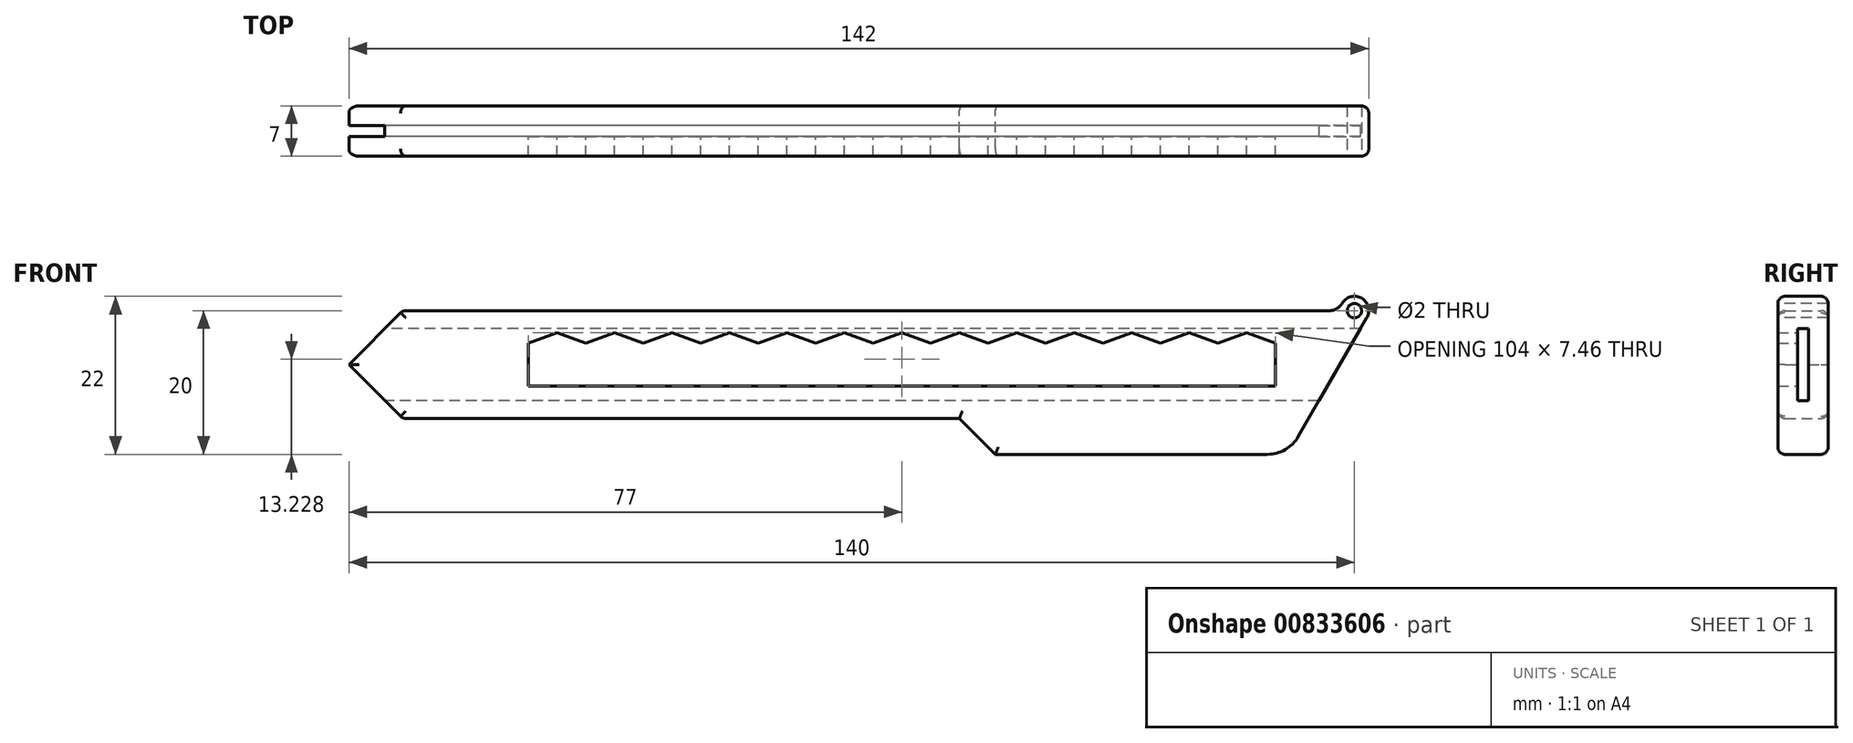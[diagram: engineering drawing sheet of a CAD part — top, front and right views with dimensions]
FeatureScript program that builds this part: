
annotation { "Feature Type Name" : "Feature", "Feature Type Description" : "" }
export const myFeature = defineFeature(function(context is Context, id is Id, definition is map)
    precondition{}
    {
        {
            var Q0;
            Q0=qCreatedBy(makeId("Front.planeOp"),FACE);
            var sketch = newSketch(context, id + "F0", { "sketchPlane" : qUnion([Q0])});
            skLineSegment(sketch, "E0.bottom", {"start": v(7.5, -7.5) * mm, "end": v(85, -7.5) * mm});
            skLineSegment(sketch, "E0.top", {"start": v(7.5, 7.5) * mm, "end": v(138, 7.5) * mm});
            skLineSegment(sketch, "E1", {"start": v(0, 0) * mm, "end": v(7.5, 7.5) * mm});
            skLineSegment(sketch, "E2", {"start": v(0, 0) * mm, "end": v(7.5, -7.5) * mm});
            skPoint(sketch, "E3.orphan", {"position": v(0, -7.5) * mm});
            skArc(sketch, "E4", {"start": v(141.73, 6.5) * mm, "mid": v(140.52, 9.43) * mm, "end": v(138, 7.5) * mm});
            skLineSegment(sketch, "E5", {"start": v(85, -7.5) * mm, "end": v(90, -12.5) * mm});
            skLineSegment(sketch, "E6", {"start": v(90, -12.5) * mm, "end": v(130.76, -12.5) * mm});
            skLineSegment(sketch, "E7", {"start": v(130.76, -12.5) * mm, "end": v(141.8, 6.62) * mm});
            skSolve(sketch);
        }
        {
            var Q0;
            Q0 = qSketchRegion(id + "F0", true);
            extrude(context, id + "F1", {"entities" : qUnion([Q0]), "endBound" : BoundingType.SYMMETRIC, "depth" : 7 * mm, "offsetDistance" : 25 * mm});
        }
        {
            var Q0;
            Q0=qCreatedBy(makeId("Front.planeOp"),FACE);
            var sketch = newSketch(context, id + "F2", { "sketchPlane" : qUnion([Q0])});
            skLineSegment(sketch, "E8", {"start": v(25, 3) * mm, "end": v(29, 4.46) * mm});
            skLineSegment(sketch, "E9", {"start": v(29, 4.46) * mm, "end": v(33, 3) * mm});
            skLineSegment(sketch, "E10", {"start": v(33, 3) * mm, "end": v(33, -3) * mm});
            skLineSegment(sketch, "E11", {"start": v(33, -3) * mm, "end": v(25, -3) * mm});
            skLineSegment(sketch, "E12", {"start": v(25, -3) * mm, "end": v(25, 3) * mm});
            skLineSegment(sketch, "E13.1.0.0", {"start": v(37, 4.46) * mm, "end": v(41, 3) * mm});
            skLineSegment(sketch, "E13.1.0.1", {"start": v(33, 3) * mm, "end": v(37, 4.46) * mm});
            skLineSegment(sketch, "E13.1.0.2", {"start": v(41, -3) * mm, "end": v(33, -3) * mm});
            skLineSegment(sketch, "E13.2.0.0", {"start": v(45, 4.46) * mm, "end": v(49, 3) * mm});
            skLineSegment(sketch, "E13.2.0.1", {"start": v(41, 3) * mm, "end": v(45, 4.46) * mm});
            skLineSegment(sketch, "E13.2.0.2", {"start": v(49, -3) * mm, "end": v(41, -3) * mm});
            skLineSegment(sketch, "E13.3.0.0", {"start": v(53, 4.46) * mm, "end": v(57, 3) * mm});
            skLineSegment(sketch, "E13.3.0.1", {"start": v(49, 3) * mm, "end": v(53, 4.46) * mm});
            skLineSegment(sketch, "E13.3.0.2", {"start": v(57, -3) * mm, "end": v(49, -3) * mm});
            skLineSegment(sketch, "E13.4.0.0", {"start": v(61, 4.46) * mm, "end": v(65, 3) * mm});
            skLineSegment(sketch, "E13.4.0.1", {"start": v(57, 3) * mm, "end": v(61, 4.46) * mm});
            skLineSegment(sketch, "E13.4.0.2", {"start": v(65, -3) * mm, "end": v(57, -3) * mm});
            skLineSegment(sketch, "E13.5.0.0", {"start": v(69, 4.46) * mm, "end": v(73, 3) * mm});
            skLineSegment(sketch, "E13.5.0.1", {"start": v(65, 3) * mm, "end": v(69, 4.46) * mm});
            skLineSegment(sketch, "E13.5.0.2", {"start": v(73, -3) * mm, "end": v(65, -3) * mm});
            skLineSegment(sketch, "E13.6.0.0", {"start": v(77, 4.46) * mm, "end": v(81, 3) * mm});
            skLineSegment(sketch, "E13.6.0.1", {"start": v(73, 3) * mm, "end": v(77, 4.46) * mm});
            skLineSegment(sketch, "E13.6.0.2", {"start": v(81, -3) * mm, "end": v(73, -3) * mm});
            skLineSegment(sketch, "E13.7.0.0", {"start": v(85, 4.46) * mm, "end": v(89, 3) * mm});
            skLineSegment(sketch, "E13.7.0.1", {"start": v(81, 3) * mm, "end": v(85, 4.46) * mm});
            skLineSegment(sketch, "E13.7.0.2", {"start": v(89, -3) * mm, "end": v(81, -3) * mm});
            skLineSegment(sketch, "E13.8.0.0", {"start": v(93, 4.46) * mm, "end": v(97, 3) * mm});
            skLineSegment(sketch, "E13.8.0.1", {"start": v(89, 3) * mm, "end": v(93, 4.46) * mm});
            skLineSegment(sketch, "E13.8.0.2", {"start": v(97, -3) * mm, "end": v(89, -3) * mm});
            skLineSegment(sketch, "E13.9.0.0", {"start": v(101, 4.46) * mm, "end": v(105, 3) * mm});
            skLineSegment(sketch, "E13.9.0.1", {"start": v(97, 3) * mm, "end": v(101, 4.46) * mm});
            skLineSegment(sketch, "E13.9.0.2", {"start": v(105, -3) * mm, "end": v(97, -3) * mm});
            skLineSegment(sketch, "E13.10.0.0", {"start": v(109, 4.46) * mm, "end": v(113, 3) * mm});
            skLineSegment(sketch, "E13.10.0.1", {"start": v(105, 3) * mm, "end": v(109, 4.46) * mm});
            skLineSegment(sketch, "E13.10.0.2", {"start": v(113, -3) * mm, "end": v(105, -3) * mm});
            skLineSegment(sketch, "E13.11.0.0", {"start": v(117, 4.46) * mm, "end": v(121, 3) * mm});
            skLineSegment(sketch, "E13.11.0.1", {"start": v(113, 3) * mm, "end": v(117, 4.46) * mm});
            skLineSegment(sketch, "E13.11.0.2", {"start": v(121, -3) * mm, "end": v(113, -3) * mm});
            skLineSegment(sketch, "E13.12.0.0", {"start": v(125, 4.46) * mm, "end": v(129, 3) * mm});
            skLineSegment(sketch, "E13.12.0.1", {"start": v(121, 3) * mm, "end": v(125, 4.46) * mm});
            skLineSegment(sketch, "E13.12.0.2", {"start": v(129, -3) * mm, "end": v(121, -3) * mm});
            skLineSegment(sketch, "E13.direction1", {"start": v(29, 4.46) * mm, "end": v(37, 4.46) * mm, "construction": true});
            skLineSegment(sketch, "E14", {"start": v(129, 3) * mm, "end": v(129, -3) * mm});
            skSolve(sketch);
        }
        {
            var Q0;
            Q0 = qSketchRegion(id + "F2", true);
            extrude(context, id + "F3", {"entities" : qUnion([Q0]), "operationType" : NewBodyOperationType.REMOVE, "endBound" : BoundingType.THROUGH_ALL, "depth" : (7 / 2) * mm, "offsetDistance" : 25 * mm});
        }
        {
            var Q0;
            Q0=qCreatedBy(makeId("Right.planeOp"),FACE);
            var sketch = newSketch(context, id + "F4", { "sketchPlane" : qUnion([Q0])});
            skLineSegment(sketch, "E15.bottom", {"start": v(-0.75, -5) * mm, "end": v(0.75, -5) * mm});
            skLineSegment(sketch, "E15.top", {"start": v(-0.75, 5) * mm, "end": v(0.75, 5) * mm});
            skLineSegment(sketch, "E15.left", {"start": v(-0.75, -5) * mm, "end": v(-0.75, 5) * mm});
            skLineSegment(sketch, "E15.right", {"start": v(0.75, -5) * mm, "end": v(0.75, 5) * mm});
            skPoint(sketch, "E15.middle", {"position": v(0, 0) * mm});
            skSolve(sketch);
        }
        {
            var Q0;
            Q0 = qSketchRegion(id + "F4", true);
            extrude(context, id + "F5", {"entities" : qUnion([Q0]), "operationType" : NewBodyOperationType.REMOVE, "endBound" : BoundingType.THROUGH_ALL, "depth" : 25 * mm, "offsetDistance" : 25 * mm});
        }
        {
            var Q0;
            Q0=makeQuery(id+"F1.opExtrude","CAP_FACE",FACE,{"disambiguationData":[OSD([sQuery(id+"F0.wireOp",EDGE,"E0.bottom"),sQuery(id+"F0.wireOp",EDGE,"E0.top"),sQuery(id+"F0.wireOp",EDGE,"E1"),sQuery(id+"F0.wireOp",EDGE,"E2"),sQuery(id+"F0.wireOp",EDGE,"E4"),sQuery(id+"F0.wireOp",EDGE,"E5"),sQuery(id+"F0.wireOp",EDGE,"E6"),sQuery(id+"F0.wireOp",EDGE,"E7")])],"isStart":false});
            var sketch = newSketch(context, id + "F6", { "sketchPlane" : qUnion([Q0])});
            skCircle(sketch, "E16", {"center": v(140, 7.5) * mm, "radius": 1 * mm});
            skSolve(sketch);
        }
        {
            var Q0;
            Q0 = qSketchRegion(id + "F6", true);
            extrude(context, id + "F7", {"entities" : qUnion([Q0]), "operationType" : NewBodyOperationType.REMOVE, "endBound" : BoundingType.THROUGH_ALL, "oppositeDirection" : true, "depth" : 25 * mm, "offsetDistance" : 25 * mm});
        }
        {
            var Q0;
            Q0=makeQuery(id+"F1.opExtrude","SWEPT_EDGE",EDGE,{"disambiguationData":[OSD([sQuery(id+"F0.wireOp",EDGE,"E0.top"),sQuery(id+"F0.wireOp",EDGE,"E4")])]});
            fillet(context, id + "F8", {"entities" : qUnion([Q0]), "radius" : 2 * mm, "tangentPropagation" : true, "allowEdgeOverflow" : false});
        }
        {
            var Q0;
            Q0=makeQuery(id+"F1.opExtrude","CAP_EDGE",EDGE,{"disambiguationData":[OSD([sQuery(id+"F0.wireOp",EDGE,"E0.top")])],"isStart":false});
            var Q1;
            Q1=makeQuery(id+"F1.opExtrude","CAP_EDGE",EDGE,{"disambiguationData":[OSD([sQuery(id+"F0.wireOp",EDGE,"E0.top")])],"isStart":true});
            var Q2;
            Q2=makeQuery(id+"F1.opExtrude","CAP_EDGE",EDGE,{"disambiguationData":[OSD([sQuery(id+"F0.wireOp",EDGE,"E6")])],"isStart":false});
            var Q3;
            Q3=makeQuery(id+"F1.opExtrude","CAP_EDGE",EDGE,{"disambiguationData":[OSD([sQuery(id+"F0.wireOp",EDGE,"E6")])],"isStart":true});
            var Q4;
            Q4=makeQuery(id+"F1.opExtrude","CAP_EDGE",EDGE,{"disambiguationData":[OSD([sQuery(id+"F0.wireOp",EDGE,"E5")])],"isStart":false});
            var Q5;
            Q5=makeQuery(id+"F1.opExtrude","CAP_EDGE",EDGE,{"disambiguationData":[OSD([sQuery(id+"F0.wireOp",EDGE,"E5")])],"isStart":true});
            var Q6;
            Q6=makeQuery(id+"F1.opExtrude","CAP_EDGE",EDGE,{"disambiguationData":[OSD([sQuery(id+"F0.wireOp",EDGE,"E0.bottom")])],"isStart":false});
            var Q7;
            Q7=makeQuery(id+"F1.opExtrude","CAP_EDGE",EDGE,{"disambiguationData":[OSD([sQuery(id+"F0.wireOp",EDGE,"E0.bottom")])],"isStart":true});
            var Q8;
            Q8=makeQuery(id+"F1.opExtrude","CAP_EDGE",EDGE,{"disambiguationData":[OSD([sQuery(id+"F0.wireOp",EDGE,"E2")])],"isStart":false});
            var Q9;
            Q9=makeQuery(id+"F1.opExtrude","CAP_EDGE",EDGE,{"disambiguationData":[OSD([sQuery(id+"F0.wireOp",EDGE,"E1")])],"isStart":false});
            var Q10;
            Q10=makeQuery(id+"F1.opExtrude","CAP_EDGE",EDGE,{"disambiguationData":[OSD([sQuery(id+"F0.wireOp",EDGE,"E1")])],"isStart":true});
            var Q11;
            Q11=makeQuery(id+"F1.opExtrude","CAP_EDGE",EDGE,{"disambiguationData":[OSD([sQuery(id+"F0.wireOp",EDGE,"E2")])],"isStart":true});
            fillet(context, id + "F9", {"entities" : qUnion([Q0, Q1, Q2, Q3, Q4, Q5, Q6, Q7, Q8, Q9, Q10, Q11]), "radius" : 1 * mm, "tangentPropagation" : true, "allowEdgeOverflow" : false});
        }
        {
            var Q0;
            Q0=makeQuery(id+"F1.opExtrude","SWEPT_EDGE",EDGE,{"disambiguationData":[OSD([sQuery(id+"F0.wireOp",EDGE,"E0.top"),sQuery(id+"F0.wireOp",EDGE,"E1")])]});
            var Q1;
            Q1=makeQuery(id+"F1.opExtrude","SWEPT_EDGE",EDGE,{"disambiguationData":[OSD([sQuery(id+"F0.wireOp",EDGE,"E0.bottom"),sQuery(id+"F0.wireOp",EDGE,"E2")])]});
            fillet(context, id + "F10", {"entities" : qUnion([Q0, Q1]), "radius" : 1 * mm, "tangentPropagation" : true, "allowEdgeOverflow" : false});
        }
        {
            var Q0;
            Q0=makeQuery(id+"F1.opExtrude","SWEPT_EDGE",EDGE,{"disambiguationData":[OSD([sQuery(id+"F0.wireOp",EDGE,"E6"),sQuery(id+"F0.wireOp",EDGE,"E7")])]});
            fillet(context, id + "F11", {"entities" : qUnion([Q0]), "radius" : 5 * mm, "tangentPropagation" : true, "allowEdgeOverflow" : false});
        }
    });
